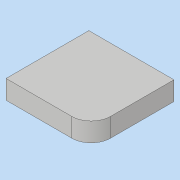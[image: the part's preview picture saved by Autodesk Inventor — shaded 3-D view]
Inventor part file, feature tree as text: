
AUTODESK INVENTOR PART (.ipt)
format: ipt  version: 2019 (Build 230136000, 136)  size: 90,112 bytes
history: native  units: mm
features: sketch x3, extrude x1, fillet x1
ambient origin geometry x8: Origin, YZ Plane, XZ Plane, XY Plane, X Axis, Y Axis, Z Axis, Center Point
bodies: Body1 (feature_tree)
feature tree (5):
  extrude  "Выдавливание2"  TaperAngle=0.0deg  [1 undecoded]
  fillet  "Сопряжение1"  Radius=42.0mm
  sketch  "Эскиз1"
  sketch  "Эскиз2"
  sketch  "Эскиз3"
note: 1 required parameter value undecoded (feature->parameter linkage not recoverable at this tier; creation-order binding heuristic only, values carry confidence <= 0.55)
